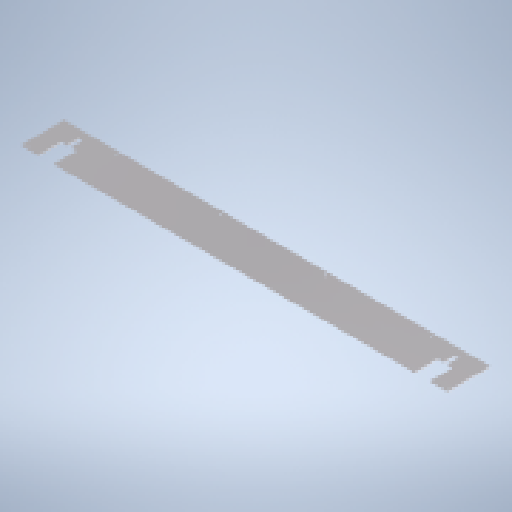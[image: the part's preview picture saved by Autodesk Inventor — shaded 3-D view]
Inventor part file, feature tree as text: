
AUTODESK INVENTOR PART (.ipt)
format: ipt  version: 2025 (Build 290162010, 162A)  size: 215,552 bytes
history: native  units: mm
features: sketch x3, hole x2, extrude x1, other x1
ambient origin geometry x8: Origin, YZ Plane, XZ Plane, XY Plane, X Axis, Y Axis, Z Axis, Center Point
bodies: Volumenkörper1 (feature_tree)
feature tree (7):
  hole  "Bohrung1"  [1 undecoded]
  extrude  "Extrusion1"  Depth=60.0mm
  hole  "Bohrung2"  [1 undecoded]
  sketch  "Skizze1"  dims[d2=270.0mm d3=10.0mm]
  sketch  "Skizze2"  dims[d4=4.3mm d5=6.0mm d6=9.4mm d7=2.0mm d8=90.0deg d9=8.0mm d10=20.594885mm d12=60.0mm]
  sketch  "Skizze3"  dims[d14=40.0mm d15=465.0mm d16=50.0mm d17=0.0mm d18=0.0mm d19=8.0mm d20=10.0mm d21=8.0mm d22=10.0mm d23=3.2mm d24=6.0mm d25=6.3mm d26=2.0mm d27=90.0deg d28=8.0mm d29=20.594885mm d33=2.0mm d34=2.0mm d35=10.0mm d36=30.0mm]
  other  "item_47308_blech-al-2mm-naturfarben_110_1100_high_1_1:1"
note: 2 required parameter values undecoded (feature->parameter linkage not recoverable at this tier; creation-order binding heuristic only, values carry confidence <= 0.55)
